# Revit family: Pressure_Regulators-Small-WATTS-LF263A_Series
name_source: partatom
category: Pipe Accessories
revit_build: Autodesk Revit 2014 (Build: 20130308_1515(x64)
units: mm (PartAtom-declared; Revit-internal decimal feet)

## types (3) — shared parameters
Connection Type = Threaded Connections
Country = United States
Description = Lead Free Small 3-Way Pressure Regulators
Height = 4 3/8"
Length = 2 1/8"
Manufacturer = WATTS
Manufacturer Product Line = Water Safety & Flow Control
Material = Lead Free-WATTS-Brass
Max. Working Pressure = 300psi (21 bar)
Price = Prices may vary. Please consult Manufacturer Representative for most up-to-date price list.
Product Documentation Link = http://media.wattswater.com
Product Page URL = http://www.watts.com
Region = North America
URL = http://www.watts.com
Warranty Information = 1 Year (Limited)
Width = 2 1/8"

## per-type parameters (varying)
| type | Connection Radius | Connection Size | Model |
| LF263A-0.25" | 1/8" | 1/4" | LF263A-1/4" |
| LF263A-0.375" | 3/16" | 3/8" | LF263A-3/8" |
| LF263A-0.5" | 1/4" | 1/2" | LF263A-1/2" |

## geometry (parser evidence)
native form markers: Sweep x1
no freeform markers — native parametric forms only
